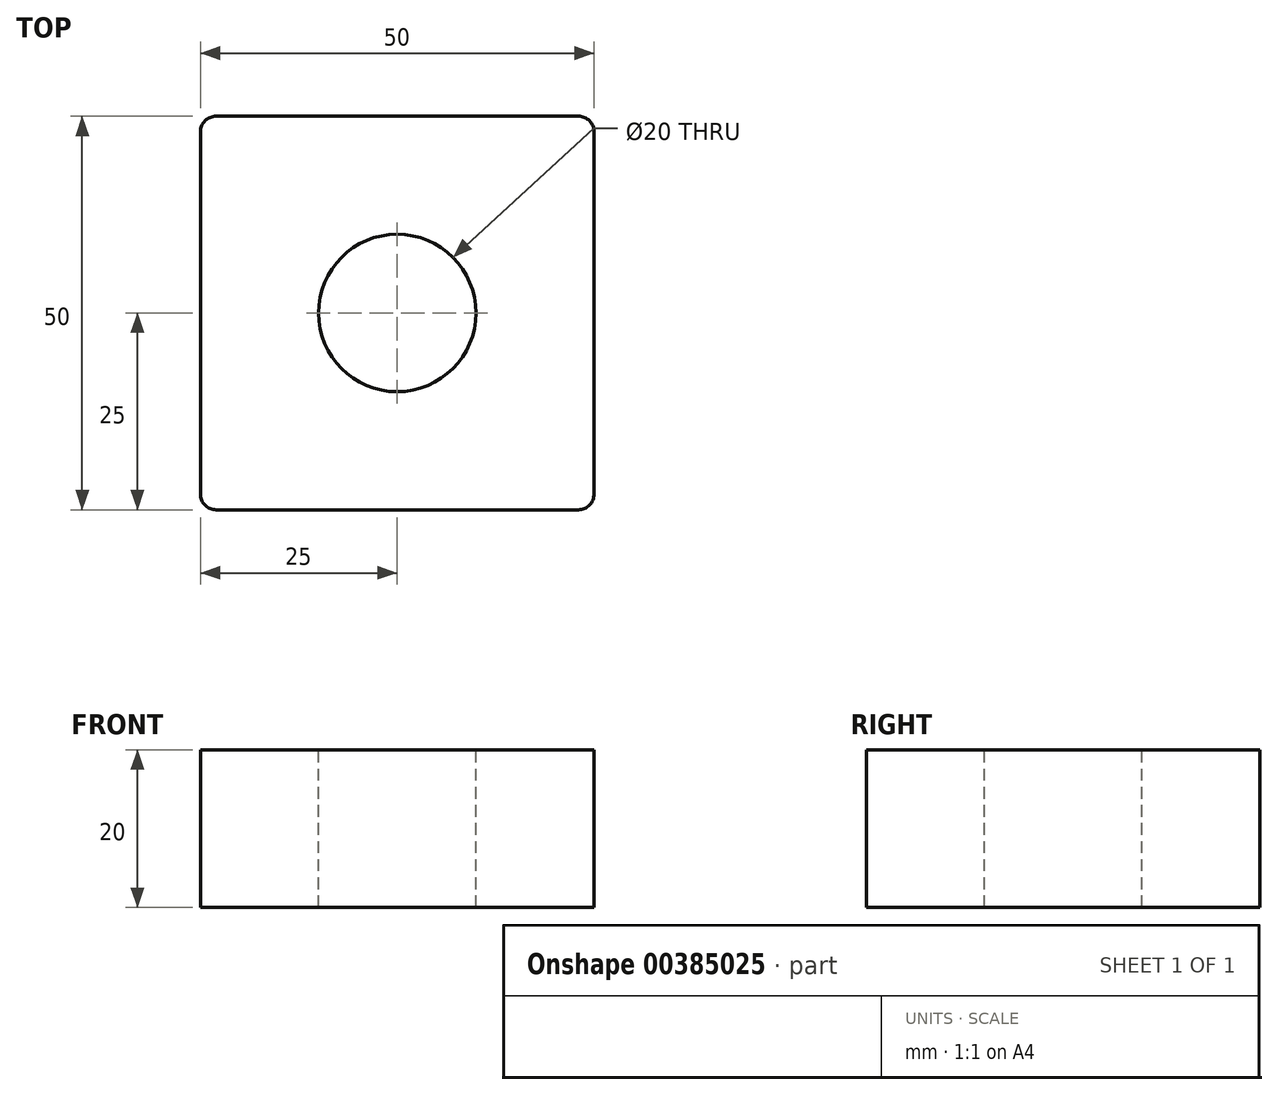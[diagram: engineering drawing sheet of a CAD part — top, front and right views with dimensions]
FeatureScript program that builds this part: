
annotation { "Feature Type Name" : "Feature", "Feature Type Description" : "" }
export const myFeature = defineFeature(function(context is Context, id is Id, definition is map)
    precondition{}
    {
        {
            var Q0;
            Q0=qCreatedBy(makeId("Top.planeOp"),FACE);
            var sketch = newSketch(context, id + "F0", { "sketchPlane" : qUnion([Q0])});
            skLineSegment(sketch, "E0.bottom", {"start": v(25, -25) * mm, "end": v(-25, -25) * mm});
            skLineSegment(sketch, "E0.top", {"start": v(25, 25) * mm, "end": v(-25, 25) * mm});
            skLineSegment(sketch, "E0.left", {"start": v(25, -25) * mm, "end": v(25, 25) * mm});
            skLineSegment(sketch, "E0.right", {"start": v(-25, -25) * mm, "end": v(-25, 25) * mm});
            skPoint(sketch, "E0.middle", {"position": v(0, 0) * mm});
            skSolve(sketch);
        }
        {
            var Q0;
            Q0 = qSketchRegion(id + "F0", true);
            extrude(context, id + "F1", {"entities" : qUnion([Q0]), "depth" : 20 * mm});
        }
        {
            var Q0;
            Q0=makeQuery(id+"F1.opExtrude","CAP_FACE",FACE,{"disambiguationData":[OSD([sQuery(id+"F0.wireOp",EDGE,"E0.bottom"),sQuery(id+"F0.wireOp",EDGE,"E0.top"),sQuery(id+"F0.wireOp",EDGE,"E0.left"),sQuery(id+"F0.wireOp",EDGE,"E0.right")])],"isStart":false});
            var sketch = newSketch(context, id + "F2", { "sketchPlane" : qUnion([Q0])});
            skCircle(sketch, "E1", {"center": v(0, 0) * mm, "radius": 10 * mm});
            skSolve(sketch);
        }
        {
            var Q0;
            Q0 = qSketchRegion(id + "F2", true);
            extrude(context, id + "F3", {"entities" : qUnion([Q0]), "operationType" : NewBodyOperationType.REMOVE, "endBound" : BoundingType.THROUGH_ALL, "oppositeDirection" : true, "depth" : 25 * mm});
        }
        {
            var Q0;
            Q0=makeQuery(id+"F1.opExtrude","SWEPT_EDGE",EDGE,{"disambiguationData":[OSD([sQuery(id+"F0.wireOp",EDGE,"E0.bottom"),sQuery(id+"F0.wireOp",EDGE,"E0.right")])]});
            var Q1;
            Q1=makeQuery(id+"F1.opExtrude","SWEPT_EDGE",EDGE,{"disambiguationData":[OSD([sQuery(id+"F0.wireOp",EDGE,"E0.bottom"),sQuery(id+"F0.wireOp",EDGE,"E0.left")])]});
            var Q2;
            Q2=makeQuery(id+"F1.opExtrude","SWEPT_EDGE",EDGE,{"disambiguationData":[OSD([sQuery(id+"F0.wireOp",EDGE,"E0.top"),sQuery(id+"F0.wireOp",EDGE,"E0.right")])]});
            var Q3;
            Q3=makeQuery(id+"F1.opExtrude","SWEPT_EDGE",EDGE,{"disambiguationData":[OSD([sQuery(id+"F0.wireOp",EDGE,"E0.top"),sQuery(id+"F0.wireOp",EDGE,"E0.left")])]});
            fillet(context, id + "F4", {"entities" : qUnion([Q0, Q1, Q2, Q3]), "radius" : 2 * mm, "tangentPropagation" : true, "allowEdgeOverflow" : false});
        }
    });
